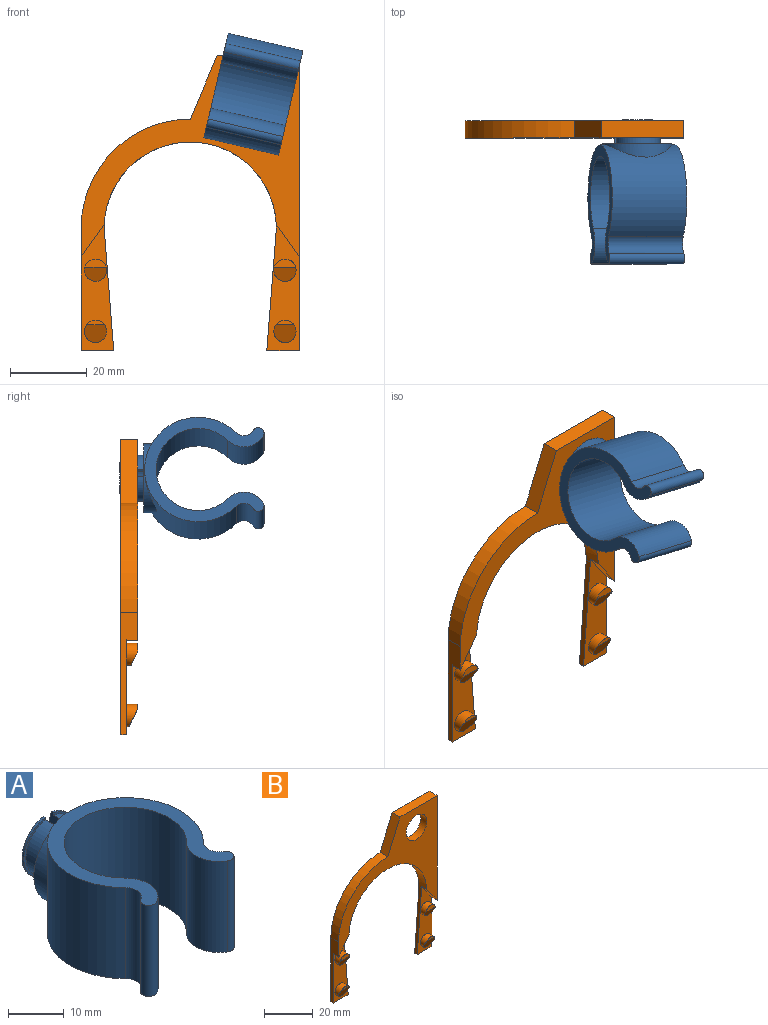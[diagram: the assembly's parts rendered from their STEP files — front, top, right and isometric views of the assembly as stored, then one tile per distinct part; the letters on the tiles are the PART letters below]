
ASSEMBLY  parts=2 mates=1
PART A: 28 faces, bbox 28x37.6x20 mm
  f0: cylinder r=4mm len=7.75mm, axis (0,-1,0), area 65.4mm2, adj f3,f18,f26,f27
  f1: cylinder r=6mm len=11.83mm, axis (0,-1,0), area 84.2mm2, adj f4,f18,f26,f27
  f2: cylinder r=6.5mm len=12.84mm, axis (0,-1,0), area 9.2mm2, adj f3,f4,f26,f27
  f3: revolved ~12.84x5.93mm, area 37.6mm2, adj f0,f2,f26,f27
  f4: plane 12.84x5.5mm, normal (0,-1,0), area 8.8mm2, adj f1,f2,f26,f27
  f5: cylinder r=14mm len=28mm, axis (0,0,-1), area 1049.3mm2, adj f6,f12,f13,f14,f15,f16,f17
  f6: cylinder r=2.86mm len=20mm, axis (0,0,-1), area 104.8mm2, adj f5,f7,f13,f14
  f7: cylinder r=1.5mm len=20mm, axis (0,0,-1), area 94.2mm2, adj f6,f8,f13,f14
  f8: cylinder r=5.86mm len=20mm, axis (0,0,-1), area 214.8mm2, adj f7,f9,f13,f14
  f9: cylinder r=11mm len=22mm, axis (0,0,-1), area 1036.7mm2, adj f8,f10,f13,f14
  f10: cylinder r=5.86mm len=20mm, axis (0,0,-1), area 214.8mm2, adj f9,f11,f13,f14
  f11: cylinder r=1.5mm len=20mm, axis (0,0,-1), area 94.2mm2, adj f10,f12,f13,f14
  f12: cylinder r=2.86mm len=20mm, axis (0,0,-1), area 104.8mm2, adj f5,f11,f13,f14
  f13: plane 31.2x28mm, normal (0,0,1), area 231.7mm2, adj f5,f6,f7,f8,f9,f10,f11,f12
  f14: plane 31.2x28mm, normal (0,0,-1), area 231.7mm2, adj f5,f6,f7,f8,f9,f10,f11,f12
  f15: plane 1.5x0.03mm, normal (0,-1,0), area 0mm2, adj f5,f16
  f16: cylinder r=9mm len=18mm, axis (0,1,0), area 103.6mm2, adj f5,f15,f17,f18
  f17: plane 1.5x0.03mm, normal (0,-1,0), area 0mm2, adj f5,f16
  f18: plane 18x18mm, normal (0,1,0), area 199.7mm2, adj f0,f1,f16,f19,f20,f24,f25,f26
  f19: cylinder r=4mm len=7.75mm, axis (0,-1,0), area 65.4mm2, adj f18,f22,f24,f25
  f20: cylinder r=6mm len=11.83mm, axis (0,-1,0), area 84.2mm2, adj f18,f23,f24,f25
  f21: cylinder r=6.5mm len=12.84mm, axis (0,-1,0), area 9.2mm2, adj f22,f23,f24,f25
  f22: revolved ~12.84x5.93mm, area 37.6mm2, adj f19,f21,f24,f25
  f23: plane 12.84x5.5mm, normal (0,-1,0), area 8.8mm2, adj f20,f21,f24,f25
  f24: plane 6.2x2.55mm, normal (-1,0,0), area 12.4mm2, adj f18,f19,f20,f21,f22,f23
  f25: plane 6.2x2.55mm, normal (-1,0,0), area 12.4mm2, adj f18,f19,f20,f21,f22,f23
  f26: plane 6.2x2.55mm, normal (1,0,0), area 12.4mm2, adj f0,f1,f2,f3,f4,f18
  f27: plane 6.2x2.55mm, normal (1,0,0), area 12.4mm2, adj f0,f1,f2,f3,f4,f18
PART B: 31 faces, bbox 57x4.5x77 mm
  f0: plane 77x57mm, normal (0,1,0), area 1330.4mm2, adj f6,f7,f8,f9,f10,f11,f12,f13
  f1: plane 33x8.5mm, normal (0,-1,0), area 159.6mm2, adj f2,f9,f10,f11,f12,f17,f25
  f2: cylinder r=2.9mm len=5.8mm, axis (0,1,0), area 42.3mm2, adj f1,f3,f24
  f3: plane 5.58x2.1mm, normal (0,-1,0), area 8.6mm2, adj f2,f24
  f4: cylinder r=2.9mm len=5.8mm, axis (0,1,0), area 42.3mm2, adj f5,f16,f23
  f5: plane 5.58x2.1mm, normal (0,-1,0), area 8.6mm2, adj f4,f23
  f6: plane 21.5x4.5mm, normal (0,0,1), area 96.7mm2, adj f0,f7,f15,f27
  f7: plane 16.5x7mm, normal (-0.92,0,0.39), area 80.7mm2, adj f0,f6,f8,f27
  f8: cylinder r=28.5mm len=28.5mm, axis (0,1,0), area 201.5mm2, adj f0,f7,f9,f27
  f9: plane 32x4.5mm, normal (-1,0,0), area 70.5mm2, adj f0,f1,f8,f10,f25,f27
  f10: plane 8.5x1.5mm, normal (0,0,-1), area 12.8mm2, adj f0,f1,f9,f11
  f11: plane 32x2.5mm, normal (1,0,0.08), area 48.1mm2, adj f0,f1,f10,f12
  f12: cylinder r=22.5mm len=45mm, axis (0,1,0), area 312.1mm2, adj f0,f1,f11,f13,f16,f25,f26,f27
  f13: plane 32x2.5mm, normal (-1,0,0.08), area 48.1mm2, adj f0,f12,f14,f16
  f14: plane 8.5x1.5mm, normal (0,0,-1), area 12.8mm2, adj f0,f13,f15,f16
  f15: plane 77x4.5mm, normal (1,0,0), area 273mm2, adj f0,f6,f14,f16,f26,f27
  f16: plane 33x8.5mm, normal (0,-1,0), area 159.6mm2, adj f4,f12,f13,f14,f15,f19,f26
  f17: cylinder r=2.9mm len=5.8mm, axis (0,1,0), area 36.4mm2, adj f1,f18,f22
  f18: plane 4.55x1.1mm, normal (0,-1,0), area 3.5mm2, adj f17,f22
  f19: cylinder r=2.9mm len=5.8mm, axis (0,1,0), area 36.4mm2, adj f16,f20,f21
  f20: plane 4.55x1.1mm, normal (0,-1,0), area 3.5mm2, adj f19,f21
  f21: plane 5.8x4.7mm, normal (0,-0.89,-0.45), area 25.6mm2, adj f19,f20
  f22: plane 5.8x4.7mm, normal (0,-0.89,-0.45), area 25.6mm2, adj f17,f18
  f23: plane 5.8x3.7mm, normal (0,-0.89,-0.45), area 19.9mm2, adj f4,f5
  f24: plane 5.8x3.7mm, normal (0,-0.89,-0.45), area 19.9mm2, adj f2,f3
  f25: plane 8.5x6.02mm, normal (0.82,0,-0.58), area 31.3mm2, adj f1,f9,f12,f27
  f26: plane 8.5x6.02mm, normal (-0.82,0,-0.58), area 31.3mm2, adj f12,f15,f16,f27
  f27: plane 57x52.5mm, normal (0,-1,0), area 993.6mm2, adj f6,f7,f8,f9,f12,f15,f25,f26
  f28: cylinder r=6mm len=12mm, axis (0,-1,0), area 131.9mm2, adj f27,f30
  f29: cylinder r=8mm len=16mm, axis (0,1,0), area 50.3mm2, adj f0,f30
  f30: plane 16x16mm, normal (0,1,0), area 88mm2, adj f28,f29
PLACE A rot(axis=(0,-1,0),76.9deg) t=(26.07,-18.16,26.12)mm
PLACE B t=(-0.16,2.09,-6.6)mm fixed
MATE revolute B.f28 <-> A.f0  axis (0,-1,0) through (16.34,1.09,28.4)mm
